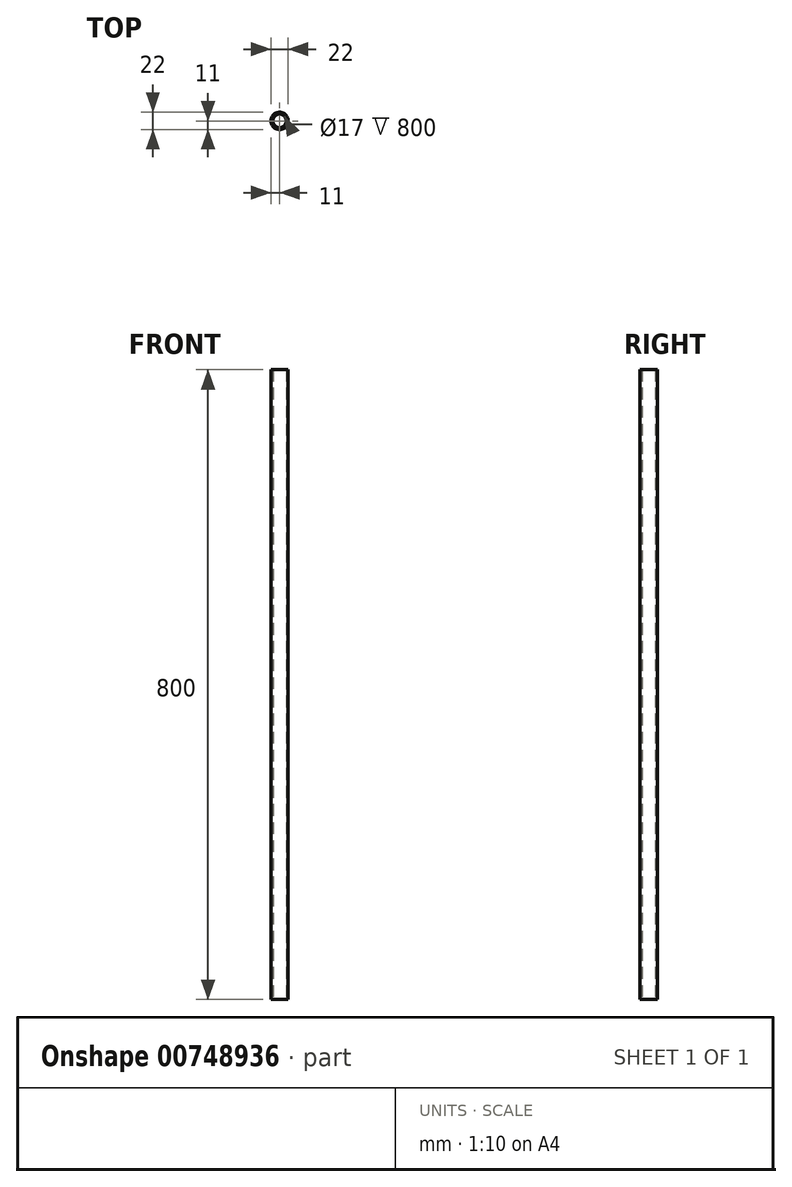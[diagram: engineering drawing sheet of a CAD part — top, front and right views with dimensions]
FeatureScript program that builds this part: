
annotation { "Feature Type Name" : "Feature", "Feature Type Description" : "" }
export const myFeature = defineFeature(function(context is Context, id is Id, definition is map)
    precondition{}
    {
        {
            var Q0;
            Q0=qCreatedBy(makeId("Top.planeOp"), FACE);
            var sketch = newSketch(context, id + "F0", { "sketchPlane" : qUnion([Q0])});
            skCircle(sketch, "E0", {"center": v(0, 0) * mm, "radius": 11 * mm});
            skCircle(sketch, "E1", {"center": v(0, 0) * mm, "radius": 8.5 * mm});
            skSolve(sketch);
        }
        {
            var Q0;
            Q0 = qSketchRegion(id + "F0", true);
            extrude(context, id + "F1", {"entities" : qUnion([Q0]), "depth" : 800 * mm, "offsetDistance" : 25 * mm, "symmetric" : true});
        }
    });
